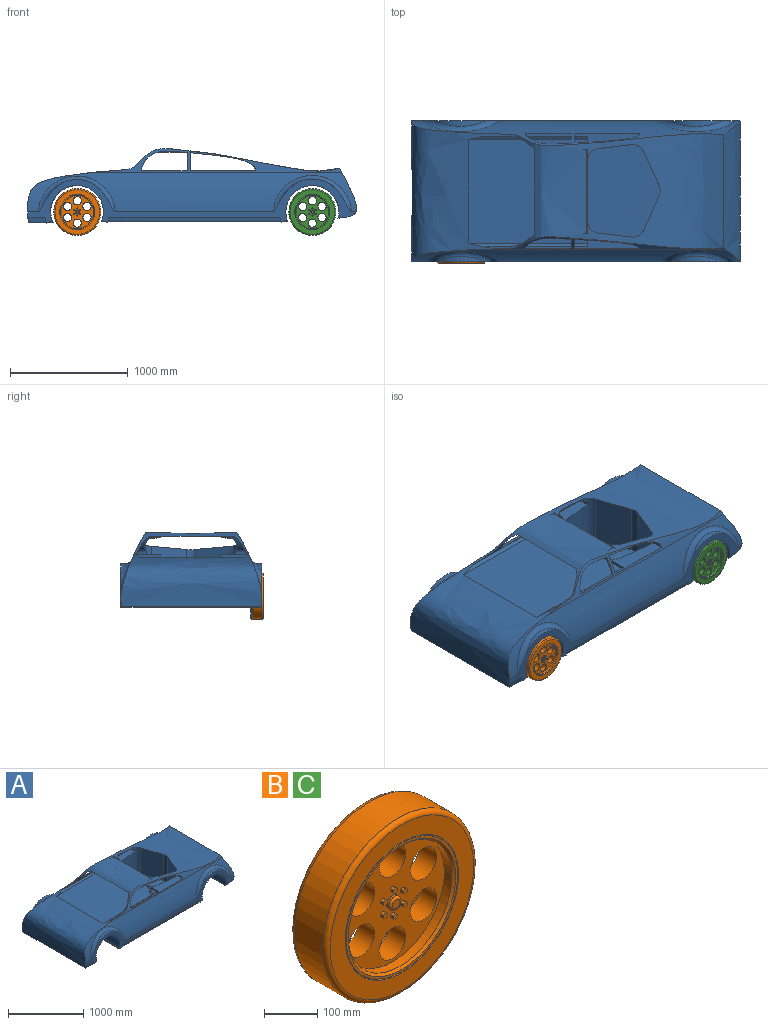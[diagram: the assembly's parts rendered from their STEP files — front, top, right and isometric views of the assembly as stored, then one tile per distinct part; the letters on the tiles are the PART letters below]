
ASSEMBLY  parts=3 mates=1
PART A: 92 faces, bbox 2862.9x1364.6x698.1 mm
  f0: extruded ~1747.68x981.04mm, area 1029483.3mm2, adj f1,f68,f69,f75,f76,f77,f78,f79
  f1: cylinder r=100mm len=99.3mm, axis (0,0,-1), area 1726.6mm2, adj f0,f2,f68,f83
  f2: extruded ~553.94x231.67mm, area 39394.3mm2, adj f1,f3,f4,f68,f82,f83,f86,f88
  f3: plane 153.51x123.37mm, normal (1,0,0), area 3098.5mm2, adj f2,f4,f86,f88
  f4: plane 553.35x231.67mm, normal (0,0,1), area 55188.9mm2, adj f2,f3,f5,f66,f67,f82,f86,f88
  f5: plane 377.98x283.95mm, normal (0.12,0.99,0), area 108078.5mm2, adj f4,f6,f67,f82
  f6: plane 788.98x617.99mm, normal (0,0,1), area 402620.6mm2, adj f5,f7,f64,f65,f67,f78,f79,f80
  f7: cylinder r=100mm len=377.98mm, axis (0,0,-1), area 54907.8mm2, adj f6,f8,f11,f64,f65
  f8: plane 553.35x223.31mm, normal (0,0,1), area 51958.8mm2, adj f7,f9,f10,f11,f64,f78,f84,f90
  f9: plane 153.51x126.96mm, normal (1,0,0), area 3641.2mm2, adj f8,f10,f84,f90
  f10: extruded ~553.94x223.31mm, area 35762.3mm2, adj f8,f9,f75,f76,f77,f78,f84,f90
  f11: plane 205.47x24.04mm, normal (-1,0,0), area 4697.5mm2, adj f7,f8,f12,f63,f84
  f12: plane 1016.4x884.49mm, normal (0,0,1), area 898990.7mm2, adj f11,f13,f62,f63,f65,f66
  f13: extruded ~1200x851.02mm, area 852761.5mm2, adj f12,f14,f19,f53,f54,f55,f56,f61
  f14: extruded ~2799.62x335.2mm, area 611407mm2, adj f13,f15,f17,f19,f89,f90
  f15: bspline ~652x314.29mm, area 47026.9mm2, adj f14,f16,f19
  f16: cylinder r=275.99mm len=419.55mm, axis (0,-1,0), area 0mm2, adj f15,f19
  f17: bspline ~660.44x318.95mm, area 47900.3mm2, adj f14,f18,f19
  f18: cylinder r=280.21mm len=429.9mm, axis (0,-1,0), area 0mm2, adj f17,f19
  f19: plane 2858.99x437.93mm, normal (0,1,0), area 182784.6mm2, adj f13,f14,f15,f16,f17,f18,f20,f21
  f20: cylinder r=275.99mm len=1200mm, axis (0,-1,0), area 6151.6mm2, adj f19,f21,f53,f54,f55,f56
  f21: plane 1200.2x48.11mm, normal (0.34,0,-0.94), area 16372mm2, adj f19,f20,f22,f23,f24,f25,f26,f56
  f22: plane 1183.38x44.09mm, normal (0,0,-1), area 52169.6mm2, adj f21,f24,f26,f27
  f23: cylinder r=225mm len=33.42mm, axis (0,-1,0), area 95.2mm2, adj f21,f24,f56
  f24: extruded ~46.35x44.09mm, area 412mm2, adj f21,f22,f23,f27,f56
  f25: cylinder r=225mm len=33.42mm, axis (0,-1,0), area 95.2mm2, adj f19,f21,f26
  f26: extruded ~46.35x44.09mm, area 412mm2, adj f19,f21,f22,f25,f27
  f27: cylinder r=225mm len=1200mm, axis (0,-1,0), area 512184mm2, adj f19,f22,f24,f26,f28,f29,f30,f56
  f28: extruded ~226.71x225mm, area 797.3mm2, adj f27,f30,f56
  f29: extruded ~226.71x225mm, area 797.3mm2, adj f19,f27,f30
  f30: cylinder r=225mm len=1200mm, axis (0,-1,0), area 533146.6mm2, adj f19,f27,f28,f29,f31,f56
  f31: plane 1200.11x48.27mm, normal (-0.33,0,-0.94), area 29436.5mm2, adj f19,f30,f32,f33,f34,f35,f36,f56
  f32: cylinder r=225mm len=1189.83mm, axis (0,-1,0), area 11155.6mm2, adj f31,f33,f34,f35
  f33: extruded ~28.56x8.79mm, area 129.3mm2, adj f31,f32,f34
  f34: plane 1186.13x28.56mm, normal (0,0,-1), area 33870.2mm2, adj f31,f32,f33,f35
  f35: extruded ~28.56x8.79mm, area 129.3mm2, adj f31,f32,f34
  f36: cylinder r=275.99mm len=1200mm, axis (0,-1,0), area 9032.9mm2, adj f19,f31,f37,f38,f39,f56
  f37: plane 1473.93x1186.13mm, normal (0,0,-1), area 1748268.5mm2, adj f36,f38,f39,f40
  f38: extruded ~1473.93x40.26mm, area 59865.4mm2, adj f36,f37,f40,f56
  f39: extruded ~1473.93x40.26mm, area 59865.4mm2, adj f19,f36,f37,f40
  f40: cylinder r=280.21mm len=1200mm, axis (0,-1,0), area 2726.9mm2, adj f19,f37,f38,f39,f41,f56
  f41: plane 1200.35x52.91mm, normal (0.31,0,-0.95), area 9081.5mm2, adj f19,f40,f42,f43,f44,f45,f46,f56
  f42: extruded ~51.09x14.71mm, area 389.9mm2, adj f41,f43,f45
  f43: cylinder r=225mm len=1192.18mm, axis (0,-1,0), area 18605.5mm2, adj f41,f42,f44,f45
  f44: extruded ~51.09x14.71mm, area 389.9mm2, adj f41,f43,f45
  f45: plane 1186.13x51.09mm, normal (0,0,-1), area 60595.2mm2, adj f41,f42,f43,f44
  f46: cylinder r=225mm len=1200mm, axis (0,-1,0), area 528154.4mm2, adj f19,f41,f47,f48,f49,f56
  f47: extruded ~225.42x225mm, area 195.5mm2, adj f46,f49,f56
  f48: extruded ~225.42x225mm, area 195.5mm2, adj f19,f46,f49
  f49: cylinder r=225mm len=1200mm, axis (0,-1,0), area 468775.2mm2, adj f19,f46,f47,f48,f50,f51,f52,f56
  f50: plane 1198.18x14.06mm, normal (0.35,0,-0.94), area 17922.4mm2, adj f49,f51,f52,f89
  f51: extruded ~74.91x12.86mm, area 359.9mm2, adj f49,f50,f56,f89
  f52: extruded ~74.91x12.86mm, area 359.9mm2, adj f19,f49,f50,f89
  f53: extruded ~156.25x46.35mm, area 6988.2mm2, adj f13,f19,f20,f54
  f54: plane 1183.38x151.67mm, normal (0,0,-1), area 179483.4mm2, adj f13,f20,f53,f55
  f55: extruded ~156.25x46.35mm, area 6988.2mm2, adj f13,f20,f54,f56
  f56: plane 2820.84x399.79mm, normal (0,-1,0), area 182786.1mm2, adj f13,f20,f21,f23,f24,f27,f28,f30
  f57: cylinder r=275.99mm len=419.55mm, axis (0,-1,0), area 0mm2, adj f56,f58
  f58: bspline ~652x314.29mm, area 47026.9mm2, adj f56,f57,f61
  f59: cylinder r=280.21mm len=429.9mm, axis (0,-1,0), area 0mm2, adj f56,f60
  f60: bspline ~660.45x320.92mm, area 47900.9mm2, adj f56,f59,f61
  f61: extruded ~2799.62x335.2mm, area 611408.7mm2, adj f13,f56,f58,f60,f88,f89
  f62: plane 1020.04x33.65mm, normal (0,0.45,0.89), area 31829.6mm2, adj f12,f13,f66,f86
  f63: plane 1020.04x33.65mm, normal (0,-0.45,0.89), area 31829.6mm2, adj f11,f12,f13,f84
  f64: plane 377.98x283.95mm, normal (0.12,-0.99,0), area 108078.5mm2, adj f6,f7,f8,f78
  f65: plane 521.59x353.94mm, normal (1,0,0), area 184611.7mm2, adj f6,f7,f12,f67
  f66: plane 217.43x24.04mm, normal (-1,0,0), area 4985mm2, adj f4,f12,f62,f67,f86
  f67: cylinder r=100mm len=377.98mm, axis (0,0,-1), area 54907.8mm2, adj f4,f5,f6,f65,f66
  f68: plane 124.82x13.29mm, normal (-1,0,0), area 1510.6mm2, adj f0,f1,f2,f86
  f69: plane 714.46x161.99mm, normal (0,0,-1), area 115732.3mm2, adj f0,f70,f84,f86
  f70: extruded ~976.57x389.55mm, area 190913.6mm2, adj f69,f71,f72,f73,f74,f84,f85,f86
  f71: plane 389.55x21.46mm, normal (0,0,1), area 8357.9mm2, adj f70,f74,f84,f90
  f72: plane 389.55x17.86mm, normal (0,0,1), area 6958.9mm2, adj f70,f73,f86,f88
  f73: plane 155.45x126.58mm, normal (-1,0,0), area 3184.1mm2, adj f70,f72,f86,f88
  f74: plane 155.45x130.17mm, normal (-1,0,0), area 3733.7mm2, adj f70,f71,f84,f90
  f75: plane 112.87x13.29mm, normal (-1,0,0), area 1353.9mm2, adj f0,f10,f76,f84
  f76: cylinder r=100mm len=99.3mm, axis (0,0,-1), area 1726.6mm2, adj f0,f10,f75,f77
  f77: plane 315.16x100.88mm, normal (0.12,-0.99,0), area 2775.1mm2, adj f0,f10,f76,f78
  f78: cylinder r=100mm len=468.62mm, axis (0,0,-1), area 54294.5mm2, adj f0,f6,f8,f10,f64,f77,f79
  f79: plane 449.11x295.46mm, normal (-0.91,-0.41,0), area 140711.5mm2, adj f0,f6,f78,f80
  f80: cylinder r=100mm len=421.8mm, axis (0,0,-1), area 36032.4mm2, adj f0,f6,f79,f81
  f81: plane 449.11x295.46mm, normal (-0.91,0.41,0), area 140711.5mm2, adj f0,f6,f80,f82
  f82: cylinder r=100mm len=468.62mm, axis (0,0,-1), area 54294.7mm2, adj f0,f2,f4,f5,f6,f81,f83
  f83: plane 315.16x100.88mm, normal (0.12,0.99,0), area 2775.1mm2, adj f0,f1,f2,f82
  f84: extruded ~876.2x164.53mm, area 26064.7mm2, adj f0,f8,f9,f10,f11,f13,f63,f69
  f85: plane 714.46x59.43mm, normal (0,0,-1), area 42460.8mm2, adj f0,f70,f84,f86
  f86: extruded ~876.2x164.53mm, area 26064.7mm2, adj f0,f2,f3,f4,f13,f62,f66,f68
  f87: cylinder r=100mm len=56.7mm, axis (0,-1,0), area 1085.7mm2, adj f0,f13,f86,f88
  f88: extruded ~2136.98x205.19mm, area 87971.9mm2, adj f0,f2,f3,f4,f13,f61,f70,f72
  f89: extruded ~1200x423.57mm, area 628872.5mm2, adj f0,f14,f19,f50,f51,f52,f56,f61
  f90: extruded ~2136.98x205.19mm, area 87971.9mm2, adj f0,f8,f9,f10,f13,f14,f70,f71
  f91: cylinder r=100mm len=56.7mm, axis (0,-1,0), area 1313.3mm2, adj f0,f13,f84,f90
PART B: 66 faces, bbox 433x95x433 mm
  f0: plane 295x295mm, normal (0,-1,0), area 4555.3mm2, adj f17,f18
  f1: cylinder r=200mm len=400mm, axis (0,1,0), area 94247.8mm2, adj f4,f5
  f2: plane 380x380mm, normal (0,1,0), area 49617.5mm2, adj f5,f16
  f3: plane 380x380mm, normal (0,-1,0), area 42725.7mm2, adj f4,f19
  f4: torus R=190mm, axis (0,-1,0), area 19380.6mm2, adj f1,f3
  f5: torus R=190mm, axis (0,-1,0), area 19380.6mm2, adj f1,f2
  f6: cylinder r=137.5mm len=275mm, axis (0,-1,0), area 17278.8mm2, adj f7,f17
  f7: plane 275x275mm, normal (0,-1,0), area 35037mm2, adj f6,f10,f11,f12,f13,f14,f15,f21
  f8: cylinder r=137.5mm len=275mm, axis (0,1,0), area 17278.8mm2, adj f9,f16
  f9: plane 275x275mm, normal (0,1,0), area 36305mm2, adj f8,f10,f11,f12,f13,f14,f15
  f10: cylinder r=35mm len=70mm, axis (0,-1,0), area 9896mm2, adj f7,f9
  f11: cylinder r=35mm len=70mm, axis (0,-1,0), area 9896mm2, adj f7,f9
  f12: cylinder r=35mm len=70mm, axis (0,-1,0), area 9896mm2, adj f7,f9
  f13: cylinder r=35mm len=70mm, axis (0,-1,0), area 9896mm2, adj f7,f9
  f14: cylinder r=35mm len=70mm, axis (0,-1,0), area 9896mm2, adj f7,f9
  f15: cylinder r=35mm len=70mm, axis (0,-1,0), area 9896mm2, adj f7,f9
  f16: cone r=137.5mm half-angle=45deg, axis (0,1,0), area 6220mm2, adj f2,f8
  f17: cone r=137.5mm half-angle=45deg, axis (0,-1,0), area 6220mm2, adj f0,f6
  f18: cylinder r=147.5mm len=295mm, axis (0,-1,0), area 4633.8mm2, adj f0,f20
  f19: cylinder r=150mm len=300mm, axis (0,-1,0), area 4712.4mm2, adj f3,f20
  f20: plane 300x300mm, normal (0,-1,0), area 2336.6mm2, adj f18,f19
  f21: plane 8x5.03mm, normal (0.55,0,0.84), area 48mm2, adj f7,f22,f26,f27
  f22: plane 8x5.35mm, normal (-0.45,0,0.89), area 48mm2, adj f7,f21,f23,f27
  f23: plane 8x5.99mm, normal (-1,0,0.05), area 48mm2, adj f7,f22,f24,f27
  f24: plane 8x5.03mm, normal (-0.55,0,-0.84), area 48mm2, adj f7,f23,f25,f27
  f25: plane 8x5.35mm, normal (0.45,0,-0.89), area 48mm2, adj f7,f24,f26,f27
  f26: plane 8x5.99mm, normal (1,0,-0.05), area 48mm2, adj f7,f21,f25,f27
  f27: plane 11.98x10.7mm, normal (0,-1,0), area 93.5mm2, adj f21,f22,f23,f24,f25,f26
  f28: plane 8x5.03mm, normal (0.55,0,0.84), area 48mm2, adj f7,f29,f33,f34
  f29: plane 8x5.35mm, normal (-0.45,0,0.89), area 48mm2, adj f7,f28,f30,f34
  f30: plane 8x5.99mm, normal (-1,0,0.05), area 48mm2, adj f7,f29,f31,f34
  f31: plane 8x5.03mm, normal (-0.55,0,-0.84), area 48mm2, adj f7,f30,f32,f34
  f32: plane 8x5.35mm, normal (0.45,0,-0.89), area 48mm2, adj f7,f31,f33,f34
  f33: plane 8x5.99mm, normal (1,0,-0.05), area 48mm2, adj f7,f28,f32,f34
  f34: plane 11.98x10.7mm, normal (0,-1,0), area 93.5mm2, adj f28,f29,f30,f31,f32,f33
  f35: plane 8x5.35mm, normal (-0.45,0,0.89), area 48mm2, adj f7,f36,f40,f41
  f36: plane 8x5.99mm, normal (-1,0,0.05), area 48mm2, adj f7,f35,f37,f41
  f37: plane 8x5.03mm, normal (-0.55,0,-0.84), area 48mm2, adj f7,f36,f38,f41
  f38: plane 8x5.35mm, normal (0.45,0,-0.89), area 48mm2, adj f7,f37,f39,f41
  f39: plane 8x5.99mm, normal (1,0,-0.05), area 48mm2, adj f7,f38,f40,f41
  f40: plane 8x5.03mm, normal (0.55,0,0.84), area 48mm2, adj f7,f35,f39,f41
  f41: plane 11.98x10.7mm, normal (0,-1,0), area 93.5mm2, adj f35,f36,f37,f38,f39,f40
  f42: plane 8x5.99mm, normal (-1,0,0.05), area 48mm2, adj f7,f43,f47,f48
  f43: plane 8x5.03mm, normal (-0.55,0,-0.84), area 48mm2, adj f7,f42,f44,f48
  f44: plane 8x5.35mm, normal (0.45,0,-0.89), area 48mm2, adj f7,f43,f45,f48
  f45: plane 8x5.99mm, normal (1,0,-0.05), area 48mm2, adj f7,f44,f46,f48
  f46: plane 8x5.03mm, normal (0.55,0,0.84), area 48mm2, adj f7,f45,f47,f48
  f47: plane 8x5.35mm, normal (-0.45,0,0.89), area 48mm2, adj f7,f42,f46,f48
  f48: plane 11.98x10.7mm, normal (0,-1,0), area 93.5mm2, adj f42,f43,f44,f45,f46,f47
  f49: plane 8x5.03mm, normal (-0.55,0,-0.84), area 48mm2, adj f7,f50,f54,f55
  f50: plane 8x5.35mm, normal (0.45,0,-0.89), area 48mm2, adj f7,f49,f51,f55
  f51: plane 8x5.99mm, normal (1,0,-0.05), area 48mm2, adj f7,f50,f52,f55
  f52: plane 8x5.03mm, normal (0.55,0,0.84), area 48mm2, adj f7,f51,f53,f55
  f53: plane 8x5.35mm, normal (-0.45,0,0.89), area 48mm2, adj f7,f52,f54,f55
  f54: plane 8x5.99mm, normal (-1,0,0.05), area 48mm2, adj f7,f49,f53,f55
  f55: plane 11.98x10.7mm, normal (0,-1,0), area 93.5mm2, adj f49,f50,f51,f52,f53,f54
  f56: plane 8x5.35mm, normal (0.45,0,-0.89), area 48mm2, adj f7,f57,f61,f62
  f57: plane 8x5.99mm, normal (1,0,-0.05), area 48mm2, adj f7,f56,f58,f62
  f58: plane 8x5.03mm, normal (0.55,0,0.84), area 48mm2, adj f7,f57,f59,f62
  f59: plane 8x5.35mm, normal (-0.45,0,0.89), area 48mm2, adj f7,f58,f60,f62
  f60: plane 8x5.99mm, normal (-1,0,0.05), area 48mm2, adj f7,f59,f61,f62
  f61: plane 8x5.03mm, normal (-0.55,0,-0.84), area 48mm2, adj f7,f56,f60,f62
  f62: plane 11.98x10.7mm, normal (0,-1,0), area 93.5mm2, adj f56,f57,f58,f59,f60,f61
  f63: cylinder r=15mm len=30mm, axis (0,1,0), area 471.2mm2, adj f7,f65
  f64: plane 20x20mm, normal (0,-1,0), area 314.2mm2, adj f65
  f65: torus R=10mm, axis (0,-1,0), area 650.6mm2, adj f63,f64
PART C: same geometry as B
PLACE A t=(-744.59,-747.41,332.47)mm
PLACE B t=(-1821.17,-662.41,332.47)mm
PLACE C t=(179.67,-652.41,332.47)mm
MATE fastened C.f1 <-> A.f46  axis (0,-1,0) through (179.67,-747.41,332.47)mm
